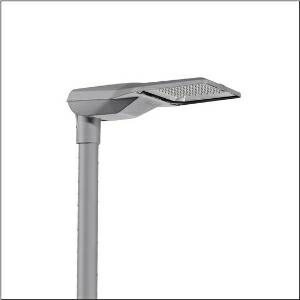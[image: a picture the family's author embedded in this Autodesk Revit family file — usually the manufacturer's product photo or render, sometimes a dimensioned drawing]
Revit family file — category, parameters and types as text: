
# Revit family: streetlight_sl_21_iq_midi___st1_5a_5xe3p31d08mb_51c0
name_source: partatom
category: Lighting Fixtures
units: mm (PartAtom-declared; Revit-internal decimal feet)

## family parameters
Cut with Voids When Loaded = No
Host = Face
Light Source = No
Part Type = Normal
Room Calculation Point = No
Round Connector Dimension = Use Diameter
Shared = No

## types (1)
- --- (1 x LED, 19170 lm, 146.7 W, 3000K)
    Apparent Load = 147 VA
    CIE Flux Codes = 22 53 95 100 100
    Color Rendering = 70
    Color Temperature = 3000K
    Default Elevation = 1800 mm
    Description = Streetlight SL 21 iQ midi, mast luminaire, primary light control with lens, of PMMA, primary optical cover: cover, of toughened safety glass, transparent, light distribution: ST1.5a, light emission: direct distribution, primary light characteristic: asymmetric, installation type: post-top, side-entry, LED, High Power LED, rated luminous flux: 19.170lm, luminous efficacy: 131lm/W, light colour: 730, colour temperature: 3000K, control gear: iQ-Comfort, control: Auto-Match, Temp-Guard, Lumen-Switch, Night-Set, Smart-Wire, Light-Fading, Desk-Remote (wireless, voltage-free reading and setting of iQ features in the workshop via application-optimized NFC function/RFID function), optimised constant luminous flux control (CLO 2.0), pre-setting: linear dimming characteristic, mains connection: 230..240V, AC, 50/60Hz, start of lifetime: 147W, end of service life: 161W, reduction: 62W, luminaire housing, of diecast aluminium, powder-coated, SITECO metallic grey (DB 702S), corrosivity category C5 high according to DIN EN ISO 12944, please order mast flange separately, inclination adjustable: 0°, 5°, 10°, 15°, sealing non-destructively replaceable, multi-level sealing system, length: 644mm, width: 335mm, height: 110mm, mast flange for spigot size: 42mm (side-entry): 5XC10008XM4, 60/48mm (side-entry/post-top): 5XC10108XM2, 76/60mm (side-entry/post-top): 5XC10108XM1, mounting height: 4..8m, protection rating (complete): IP66, insulation class (complete): insulation class II (safety insulation), certification: CE, ENEC, ENEC+, VDE, impact resistance: IK10, permissible operating ambient temperature for outdoor applications: -40..+50°C, standard-compliant lighting for roads and squares, packaging unit: 1 piece

Light Distribution: ST1.5a
    Height = 111 mm
    Lamp = 1 x LED
    Lamp Light Flux = 19170 lm
    Lamp Power = 146.7 W
    Lamp count = 1
    Length = 644 mm
    Luminous efficacy = 131 lm/W
    Manufacturer = Siteco
    ModVariant = No
    Model = 5XE3P31D08MB
    Number of Poles = 1
    OnlyDefault = Yes
    Power Factor = 1
    Product Name = Streetlight SL 21 iQ midi | ST1.5a
    Product group = mast luminaire | pylon top
    ProductGroupID = 6100
    Protection Class = Protection class II
    Protection Degree = IP 66
    RLX_Detail_Level = 1
    RLX_Emergency_Light_Flux = 0 lm
    RLX_Emergency_Type = 0
    RLX_Emergency_Type_DB = No
    RlxData = <blob elided: 30457 chars, md5=bbffd7c1>
    Socket = socket
    Standby Power = 0 W
    System Light Flux = 19169 lm
    System Power = 147 W
    Type Comments = factory setting: luminous flux: 100 % | dim-lin: 254 | 753 mA
    Type Image = l_1004298.jpg
    URL = http://relux.com
    VarID = @adj_175811
    Voltage = 0 V
    Weight = 0.00 kg
    Width = 336 mm

## geometry (parser evidence)
native form markers: Blend x4, Sweep x8
no freeform markers — native parametric forms only
